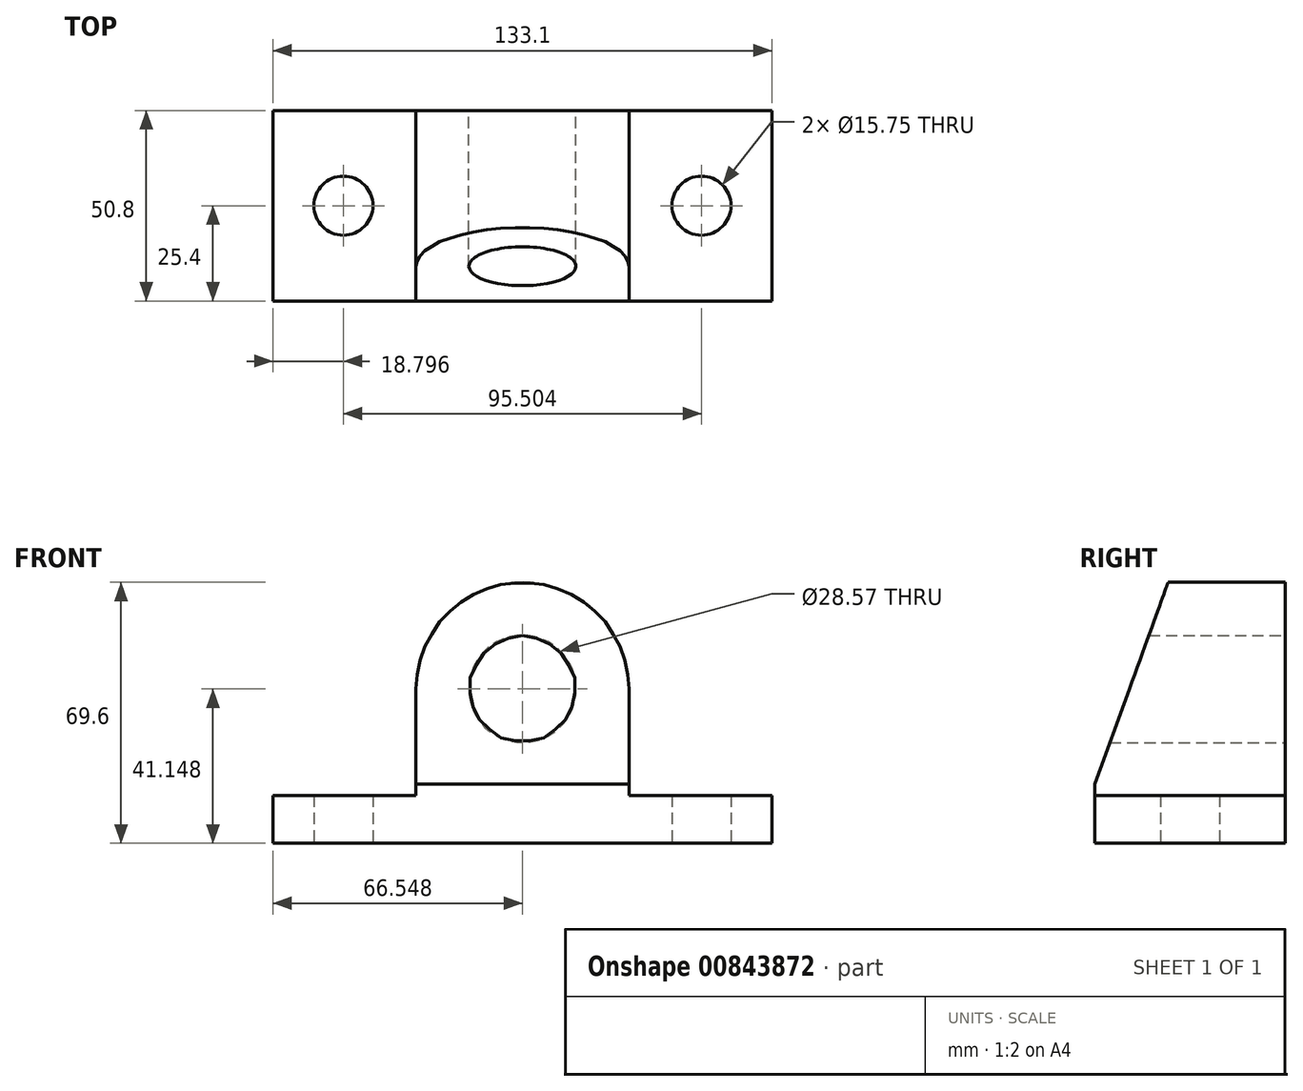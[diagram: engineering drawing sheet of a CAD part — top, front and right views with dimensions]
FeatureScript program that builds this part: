
annotation { "Feature Type Name" : "Feature", "Feature Type Description" : "" }
export const myFeature = defineFeature(function(context is Context, id is Id, definition is map)
    precondition{}
    {
        {
            var Q0;
            Q0=qCreatedBy(makeId("Right.planeOp"),FACE);
            var sketch = newSketch(context, id + "F0", { "sketchPlane" : qUnion([Q0])});
            skLineSegment(sketch, "E0", {"start": v(0, 0) * mm, "end": v(50.8, 0) * mm});
            skLineSegment(sketch, "E1", {"start": v(50.8, 0) * mm, "end": v(50.8, 12.7) * mm});
            skLineSegment(sketch, "E2", {"start": v(50.8, 12.7) * mm, "end": v(0, 12.7) * mm});
            skLineSegment(sketch, "E3", {"start": v(0, 12.7) * mm, "end": v(0, 0) * mm});
            skLineSegment(sketch, "E4", {"start": v(0, 0) * mm, "end": v(0, 15.75) * mm});
            skLineSegment(sketch, "E5", {"start": v(0, 15.75) * mm, "end": v(50.8, 15.75) * mm});
            skLineSegment(sketch, "E6", {"start": v(50.8, 15.75) * mm, "end": v(50.8, 12.7) * mm});
            skLineSegment(sketch, "E7", {"start": v(50.8, 15.75) * mm, "end": v(50.8, 69.6) * mm});
            skLineSegment(sketch, "E8", {"start": v(50.8, 69.6) * mm, "end": v(0, 69.6) * mm});
            skLineSegment(sketch, "E9", {"start": v(0, 69.6) * mm, "end": v(0, 15.75) * mm});
            skLineSegment(sketch, "E10", {"start": v(0, 15.75) * mm, "end": v(19.6, 69.6) * mm});
            skSolve(sketch);
        }
        {
            var Q0;
            {var subQ0=sQuery(id+"F0.wireOp",EDGE,"E0");Q0=makeQuery(id+"F0.imprint","IMPRINT",FACE,{"disambiguationData":[TD([[makeQuery(id+"F0.imprint","IMPRINT",EDGE,{"derivedFrom":subQ0}),1.0]])]});}
            var Q1;
            Q1=makeQuery(id+"F0.imprint","IMPRINT",FACE,{"disambiguationData":[TD([[makeQuery(id+"F0.imprint","IMPRINT",EDGE,{"derivedFrom":sQuery(id+"F0.wireOp",EDGE,"E5")}),1.0]])]});
            var Q2;
            {var subQ0=sQuery(id+"F0.wireOp",EDGE,"E2");Q2=makeQuery(id+"F0.imprint","IMPRINT",FACE,{"disambiguationData":[TD([[makeQuery(id+"F0.imprint","IMPRINT",EDGE,{"derivedFrom":subQ0}),-1.0]])]});}
            extrude(context, id + "F1", {"entities" : qUnion([Q0, Q1, Q2]), "depth" : 56.9 * mm, "offsetDistance" : 25.4 * mm});
        }
        {
            var Q0;
            {var subQ0=sQuery(id+"F0.wireOp",EDGE,"E0");Q0=makeQuery(id+"F0.imprint","IMPRINT",FACE,{"disambiguationData":[TD([[makeQuery(id+"F0.imprint","IMPRINT",EDGE,{"derivedFrom":subQ0}),1.0]])]});}
            extrude(context, id + "F2", {"entities" : qUnion([Q0]), "operationType" : NewBodyOperationType.ADD, "depth" : 95 * mm, "offsetDistance" : 25.4 * mm});
        }
        {
            var Q0;
            {var subQ0=sQuery(id+"F0.wireOp",EDGE,"E0");Q0=makeQuery(id+"F0.imprint","IMPRINT",FACE,{"disambiguationData":[TD([[makeQuery(id+"F0.imprint","IMPRINT",EDGE,{"derivedFrom":subQ0}),1.0]])]});}
            extrude(context, id + "F3", {"entities" : qUnion([Q0]), "operationType" : NewBodyOperationType.ADD, "oppositeDirection" : true, "depth" : 38.1 * mm, "offsetDistance" : 25.4 * mm});
        }
        {
            var Q0;
            Q0=makeQuery(id+"F1.opExtrude","CAP_EDGE",EDGE,{"disambiguationData":[OSD([sQuery(id+"F0.wireOp",EDGE,"E8")])],"isStart":true});
            var Q1;
            Q1=makeQuery(id+"F1.opExtrude","CAP_EDGE",EDGE,{"disambiguationData":[OSD([sQuery(id+"F0.wireOp",EDGE,"E8")])],"isStart":false});
            fillet(context, id + "F4", {"entities" : qUnion([Q0, Q1]), "radius" : 28.45 * mm, "tangentPropagation" : true, "allowEdgeOverflow" : false});
        }
        {
            var Q0;
            {var subQ0=sQuery(id+"F0.wireOp",EDGE,"E1");Q0=makeQuery(id+"F3.boolean.opBoolean","MERGE",FACE,{"derivedFrom":[makeQuery(id+"F2.boolean.opBoolean","MERGE",FACE,{"derivedFrom":[makeQuery(id+"F1.opExtrude","SWEPT_FACE",FACE,{"disambiguationData":[OSD([subQ0,sQuery(id+"F0.wireOp",EDGE,"E6"),sQuery(id+"F0.wireOp",EDGE,"E7")])]}),makeQuery(id+"F2.opExtrude","SWEPT_FACE",FACE,{"disambiguationData":[OSD([subQ0])]})]}),makeQuery(id+"F3.opExtrude","SWEPT_FACE",FACE,{"disambiguationData":[OSD([subQ0])]})]});}
            var sketch = newSketch(context, id + "F5", { "sketchPlane" : qUnion([Q0])});
            skLineSegment(sketch, "E11", {"start": v(-95, 0) * mm, "end": v(-95, 41.15) * mm});
            skLineSegment(sketch, "E12", {"start": v(-95, 41.15) * mm, "end": v(0, 41.15) * mm});
            skLineSegment(sketch, "E13", {"start": v(0, 41.15) * mm, "end": v(-56.9, 41.15) * mm});
            skCircle(sketch, "E14", {"center": v(-28.45, 41.15) * mm, "radius": 14.29 * mm});
            skSolve(sketch);
        }
        {
            var Q0;
            Q0 = qSketchRegion(id + "F5", true);
            extrude(context, id + "F6", {"entities" : qUnion([Q0]), "operationType" : NewBodyOperationType.REMOVE, "oppositeDirection" : true, "depth" : 51.05 * mm, "offsetDistance" : 25.4 * mm});
        }
        {
            var Q0;
            {var subQ0=sQuery(id+"F0.wireOp",EDGE,"E0");Q0=makeQuery(id+"F3.boolean.opBoolean","MERGE",FACE,{"derivedFrom":[makeQuery(id+"F2.boolean.opBoolean","MERGE",FACE,{"derivedFrom":[makeQuery(id+"F1.opExtrude","SWEPT_FACE",FACE,{"disambiguationData":[OSD([subQ0])]}),makeQuery(id+"F2.opExtrude","SWEPT_FACE",FACE,{"disambiguationData":[OSD([subQ0])]})]}),makeQuery(id+"F3.opExtrude","SWEPT_FACE",FACE,{"disambiguationData":[OSD([subQ0])]})]});}
            var sketch = newSketch(context, id + "F7", { "sketchPlane" : qUnion([Q0])});
            skLineSegment(sketch, "E15", {"start": v(-38.1, 0) * mm, "end": v(-38.1, -25.4) * mm});
            skLineSegment(sketch, "E16", {"start": v(-38.1, -25.4) * mm, "end": v(-19.3, -25.4) * mm});
            skLineSegment(sketch, "E17", {"start": v(-19.3, -25.4) * mm, "end": v(76.2, -25.4) * mm});
            skLineSegment(sketch, "E18", {"start": v(76.2, -25.4) * mm, "end": v(95, -25.4) * mm});
            skCircle(sketch, "E19", {"center": v(-19.3, -25.4) * mm, "radius": 7.87 * mm});
            skCircle(sketch, "E20", {"center": v(76.2, -25.4) * mm, "radius": 7.87 * mm});
            skLineSegment(sketch, "E21", {"start": v(28.45, -25.4) * mm, "end": v(-19.3, -25.4) * mm});
            skSolve(sketch);
        }
        {
            var Q0;
            Q0 = qSketchRegion(id + "F7", true);
            extrude(context, id + "F8", {"entities" : qUnion([Q0]), "operationType" : NewBodyOperationType.REMOVE, "oppositeDirection" : true, "depth" : 42.42 * mm, "offsetDistance" : 25.4 * mm});
        }
    });
